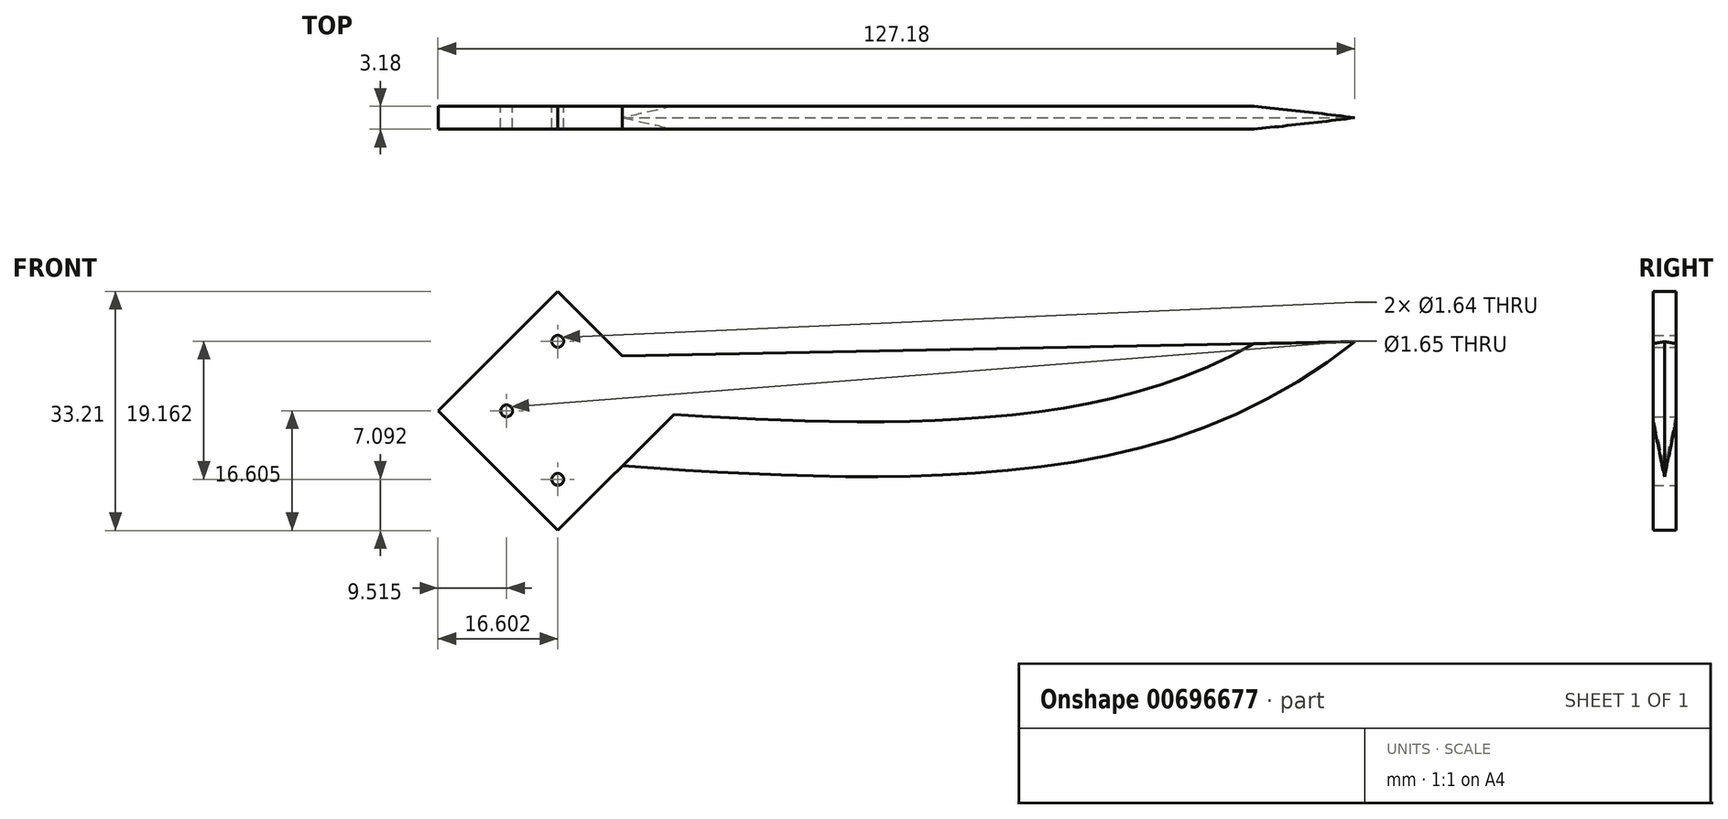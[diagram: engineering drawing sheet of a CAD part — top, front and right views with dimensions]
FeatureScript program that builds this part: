
annotation { "Feature Type Name" : "Feature", "Feature Type Description" : "" }
export const myFeature = defineFeature(function(context is Context, id is Id, definition is map)
    precondition{}
    {
        {
            var Q0;
            Q0=qCreatedBy(makeId("Front.planeOp"),FACE);
            var sketch = newSketch(context, id + "F0", { "sketchPlane" : qUnion([Q0])});
            skLineSegment(sketch, "E0", {"start": v(-51.37, 22.44) * mm, "end": v(-44.42, 29.4) * mm});
            skLineSegment(sketch, "E1", {"start": v(-44.42, 29.4) * mm, "end": v(-35.44, 20.41) * mm});
            skLineSegment(sketch, "E2", {"start": v(-51.5, 3.28) * mm, "end": v(-44.42, -3.8) * mm});
            skLineSegment(sketch, "E3", {"start": v(-44.42, -3.8) * mm, "end": v(-35.44, 5.17) * mm});
            skCircle(sketch, "E4", {"center": v(-44.42, 22.44) * mm, "radius": 0.82 * mm});
            skCircle(sketch, "E5", {"center": v(-44.42, 3.28) * mm, "radius": 0.82 * mm});
            skLineSegment(sketch, "E6", {"start": v(-51.37, 22.44) * mm, "end": v(-61.02, 12.8) * mm});
            skLineSegment(sketch, "E7", {"start": v(-51.5, 3.28) * mm, "end": v(-61.02, 12.8) * mm});
            skLineSegment(sketch, "E8", {"start": v(-35.44, 20.41) * mm, "end": v(66.16, 22.4) * mm});
            skFitSpline(sketch, "E9", {"points": [v(-35.44, 5.17) * mm, v(23.69, 5.17) * mm, v(66.16, 22.4) * mm], "startDerivative": vector(115.98, -8.64) * mm, "endDerivative": vector(84.29, 66.07) * mm});
            skCircle(sketch, "E10", {"center": v(-51.5, 12.8) * mm, "radius": 0.82 * mm});
            skSolve(sketch);
        }
        {
            var Q0;
            Q0=makeQuery(id+"F0.imprint","IMPRINT",FACE,{"disambiguationData":[TD([[makeQuery(id+"F0.imprint","IMPRINT",EDGE,{"derivedFrom":sQuery(id+"F0.wireOp",EDGE,"E0")}),-1.0]])]});
            extrude(context, id + "F1", {"entities" : qUnion([Q0]), "depth" : 3.17 * mm, "offsetDistance" : 25.4 * mm});
        }
        {
            var Q0;
            Q0=makeQuery(id+"F1.opExtrude","CAP_EDGE",EDGE,{"disambiguationData":[OSD([sQuery(id+"F0.wireOp",EDGE,"00c3c85d-c45e-48a6-aed7-b82995e2ba4a")])],"isStart":true});
            var Q1;
            Q1=makeQuery(id+"F1.opExtrude","CAP_EDGE",EDGE,{"disambiguationData":[OSD([sQuery(id+"F0.wireOp",EDGE,"00c3c85d-c45e-48a6-aed7-b82995e2ba4a")])],"isStart":false});
            var Q2;
            Q2=makeQuery(id+"F1.opExtrude","CAP_EDGE",EDGE,{"disambiguationData":[OSD([sQuery(id+"F0.wireOp",EDGE,"E9")])],"isStart":false});
            var Q3;
            Q3=makeQuery(id+"F1.opExtrude","CAP_EDGE",EDGE,{"disambiguationData":[OSD([sQuery(id+"F0.wireOp",EDGE,"E9")])],"isStart":true});
            chamfer(context, id + "F2", {"entities" : qUnion([Q0, Q1, Q2, Q3]), "chamferType" : ChamferType.TWO_OFFSETS, "width1" : 7.62 * mm, "oppositeDirection" : false, "width2" : 1.59 * mm, "tangentPropagation" : true});
        }
    });
